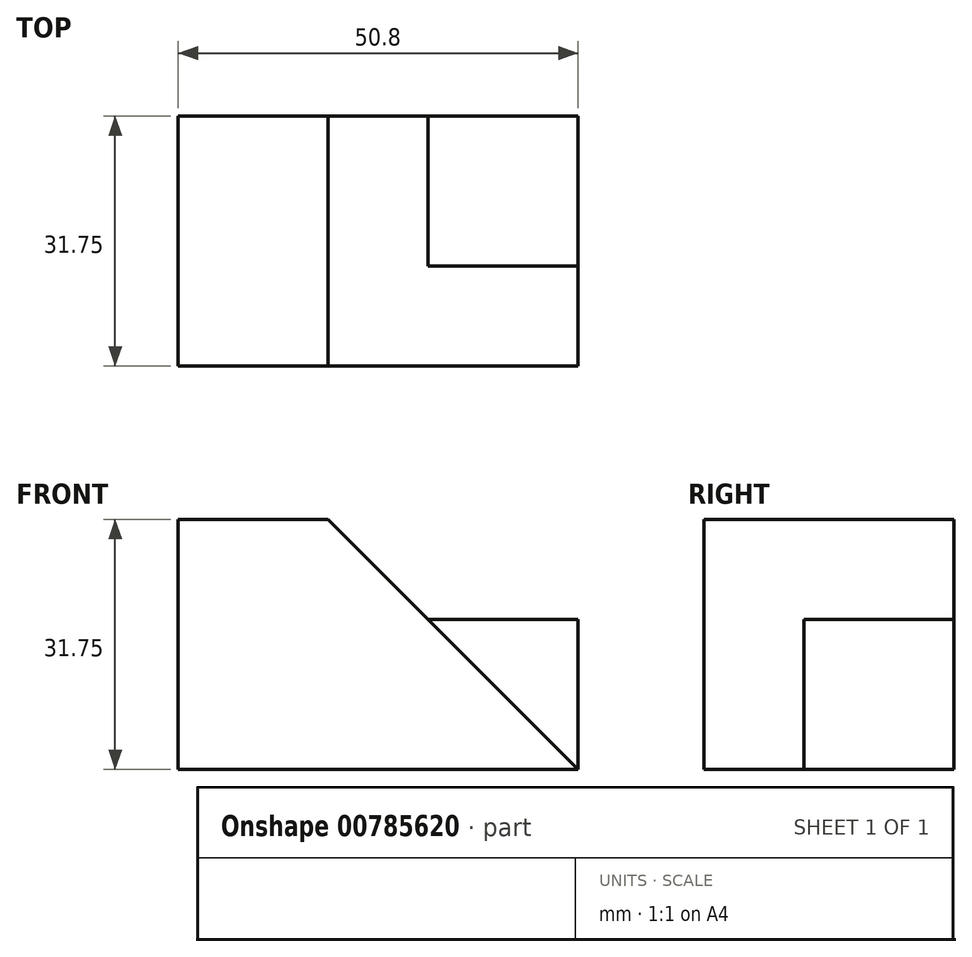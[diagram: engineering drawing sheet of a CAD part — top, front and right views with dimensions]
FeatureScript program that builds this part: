
annotation { "Feature Type Name" : "Feature", "Feature Type Description" : "" }
export const myFeature = defineFeature(function(context is Context, id is Id, definition is map)
    precondition{}
    {
        {
            var Q0;
            Q0=qCreatedBy(makeId("Front.planeOp"),FACE);
            var sketch = newSketch(context, id + "F0", { "sketchPlane" : qUnion([Q0])});
            skLineSegment(sketch, "E0", {"start": v(0, 0) * mm, "end": v(50.8, 0) * mm});
            skLineSegment(sketch, "E1", {"start": v(0, 0) * mm, "end": v(0, 31.75) * mm});
            skLineSegment(sketch, "E2", {"start": v(0, 31.75) * mm, "end": v(19.05, 31.75) * mm});
            skLineSegment(sketch, "E3", {"start": v(50.8, 0) * mm, "end": v(50.8, 19.05) * mm});
            skLineSegment(sketch, "E4", {"start": v(50.8, 19.05) * mm, "end": v(31.75, 19.05) * mm});
            skLineSegment(sketch, "E5", {"start": v(31.75, 19.05) * mm, "end": v(19.05, 31.75) * mm});
            skSolve(sketch);
        }
        {
            var Q0;
            Q0=makeQuery(id+"F0.imprint","IMPRINT",FACE,{"disambiguationData":[TD([[makeQuery(id+"F0.imprint","IMPRINT",EDGE,{"derivedFrom":sQuery(id+"F0.wireOp",EDGE,"E0")}),1.0]])]});
            extrude(context, id + "F1", {"entities" : qUnion([Q0]), "depth" : 31.75 * mm, "offsetDistance" : 25.4 * mm});
        }
        {
            var Q0;
            Q0=makeQuery(id+"F1.opExtrude","CAP_FACE",FACE,{"disambiguationData":[OSD([sQuery(id+"F0.wireOp",EDGE,"E0"),sQuery(id+"F0.wireOp",EDGE,"E1"),sQuery(id+"F0.wireOp",EDGE,"E2"),sQuery(id+"F0.wireOp",EDGE,"E3"),sQuery(id+"F0.wireOp",EDGE,"E4"),sQuery(id+"F0.wireOp",EDGE,"E5")])],"isStart":false});
            var sketch = newSketch(context, id + "F2", { "sketchPlane" : qUnion([Q0])});
            skLineSegment(sketch, "E6", {"start": v(31.75, 19.05) * mm, "end": v(50.8, 0) * mm});
            skSolve(sketch);
        }
        {
            var Q0;
            Q0 = qSketchRegion(id + "F2", true);
            var Q1;
            Q1=makeQuery(id+"F2.imprint","IMPRINT",FACE,{"disambiguationData":[TD([[makeQuery(id+"F2.imprint","IMPRINT",EDGE,{"derivedFrom":sQuery(id+"F2.wireOp",EDGE,"E6")}),1.0]])]});
            extrude(context, id + "F3", {"entities" : qUnion([Q0, Q1]), "operationType" : NewBodyOperationType.REMOVE, "oppositeDirection" : true, "depth" : 12.7 * mm, "offsetDistance" : 25.4 * mm});
        }
    });
